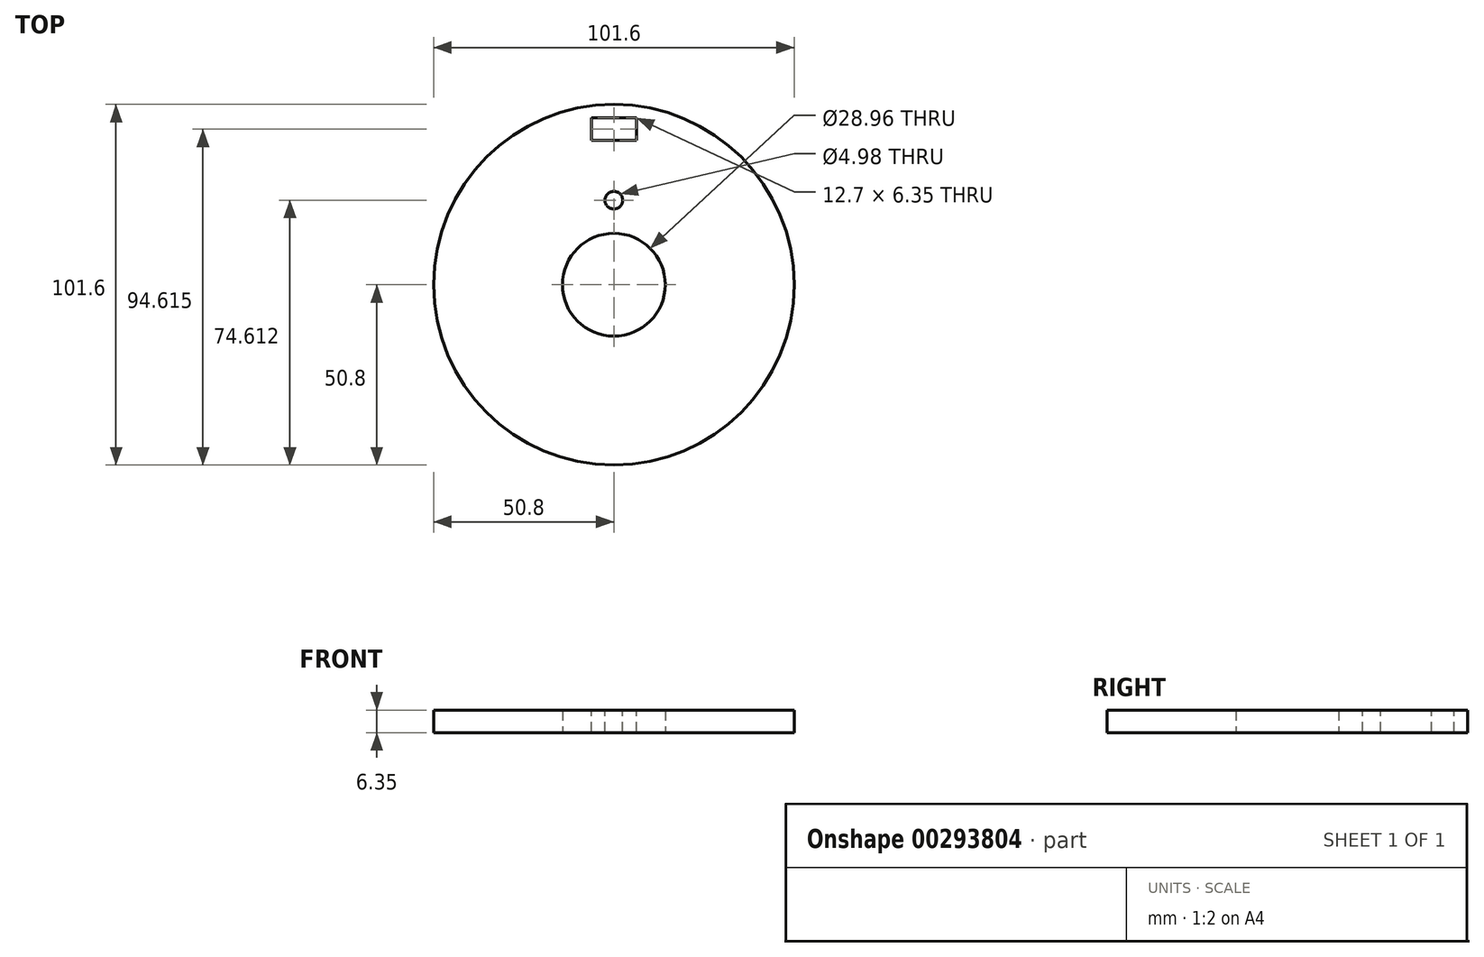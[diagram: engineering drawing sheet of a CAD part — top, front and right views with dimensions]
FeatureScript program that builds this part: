
annotation { "Feature Type Name" : "Feature", "Feature Type Description" : "" }
export const myFeature = defineFeature(function(context is Context, id is Id, definition is map)
    precondition{}
    {
        {
            var Q0;
            Q0=qCreatedBy(makeId("Top.planeOp"),FACE);
            var sketch = newSketch(context, id + "F0", { "sketchPlane" : qUnion([Q0])});
            skCircle(sketch, "E0", {"center": v(0, 0) * mm, "radius": 50.8 * mm});
            skCircle(sketch, "E1", {"center": v(0, 0) * mm, "radius": 14.48 * mm});
            skSolve(sketch);
        }
        {
            var Q0;
            Q0 = qSketchRegion(id + "F0", true);
            extrude(context, id + "F1", {"entities" : qUnion([Q0]), "depth" : 6.35 * mm});
        }
        {
            var Q0;
            Q0=makeQuery(id+"F1.opExtrude","CAP_FACE",FACE,{"disambiguationData":[OSD([sQuery(id+"F0.wireOp",EDGE,"E0"),sQuery(id+"F0.wireOp",EDGE,"E1")])],"isStart":false});
            var sketch = newSketch(context, id + "F2", { "sketchPlane" : qUnion([Q0])});
            skCircle(sketch, "E2", {"center": v(0, 0) * mm, "radius": 23.81 * mm, "construction": true});
            skCircle(sketch, "E3", {"center": v(0, 23.81) * mm, "radius": 2.49 * mm});
            skSolve(sketch);
        }
        {
            var Q0;
            Q0 = qSketchRegion(id + "F2", true);
            extrude(context, id + "F3", {"entities" : qUnion([Q0]), "operationType" : NewBodyOperationType.REMOVE, "oppositeDirection" : true, "depth" : 25.4 * mm});
        }
        {
            var Q0;
            Q0=makeQuery(id+"F1.opExtrude","CAP_FACE",FACE,{"disambiguationData":[OSD([sQuery(id+"F0.wireOp",EDGE,"E0"),sQuery(id+"F0.wireOp",EDGE,"E1")])],"isStart":false});
            var sketch = newSketch(context, id + "F4", { "sketchPlane" : qUnion([Q0])});
            skLineSegment(sketch, "E4.bottom", {"start": v(6.35, 47) * mm, "end": v(-6.35, 47) * mm});
            skLineSegment(sketch, "E4.top", {"start": v(6.35, 40.64) * mm, "end": v(-6.35, 40.64) * mm});
            skLineSegment(sketch, "E4.left", {"start": v(6.35, 47) * mm, "end": v(6.35, 40.64) * mm});
            skLineSegment(sketch, "E4.right", {"start": v(-6.35, 47) * mm, "end": v(-6.35, 40.64) * mm});
            skPoint(sketch, "E4.middle", {"position": v(0, 43.82) * mm});
            skSolve(sketch);
        }
        {
            var Q0;
            Q0=makeQuery(id+"F4.imprint","IMPRINT",FACE,{"disambiguationData":[TD([[makeQuery(id+"F4.imprint","IMPRINT",EDGE,{"derivedFrom":sQuery(id+"F4.wireOp",EDGE,"E4.bottom")}),1.0]])]});
            extrude(context, id + "F5", {"entities" : qUnion([Q0]), "operationType" : NewBodyOperationType.REMOVE, "oppositeDirection" : true, "depth" : 25.4 * mm});
        }
    });
